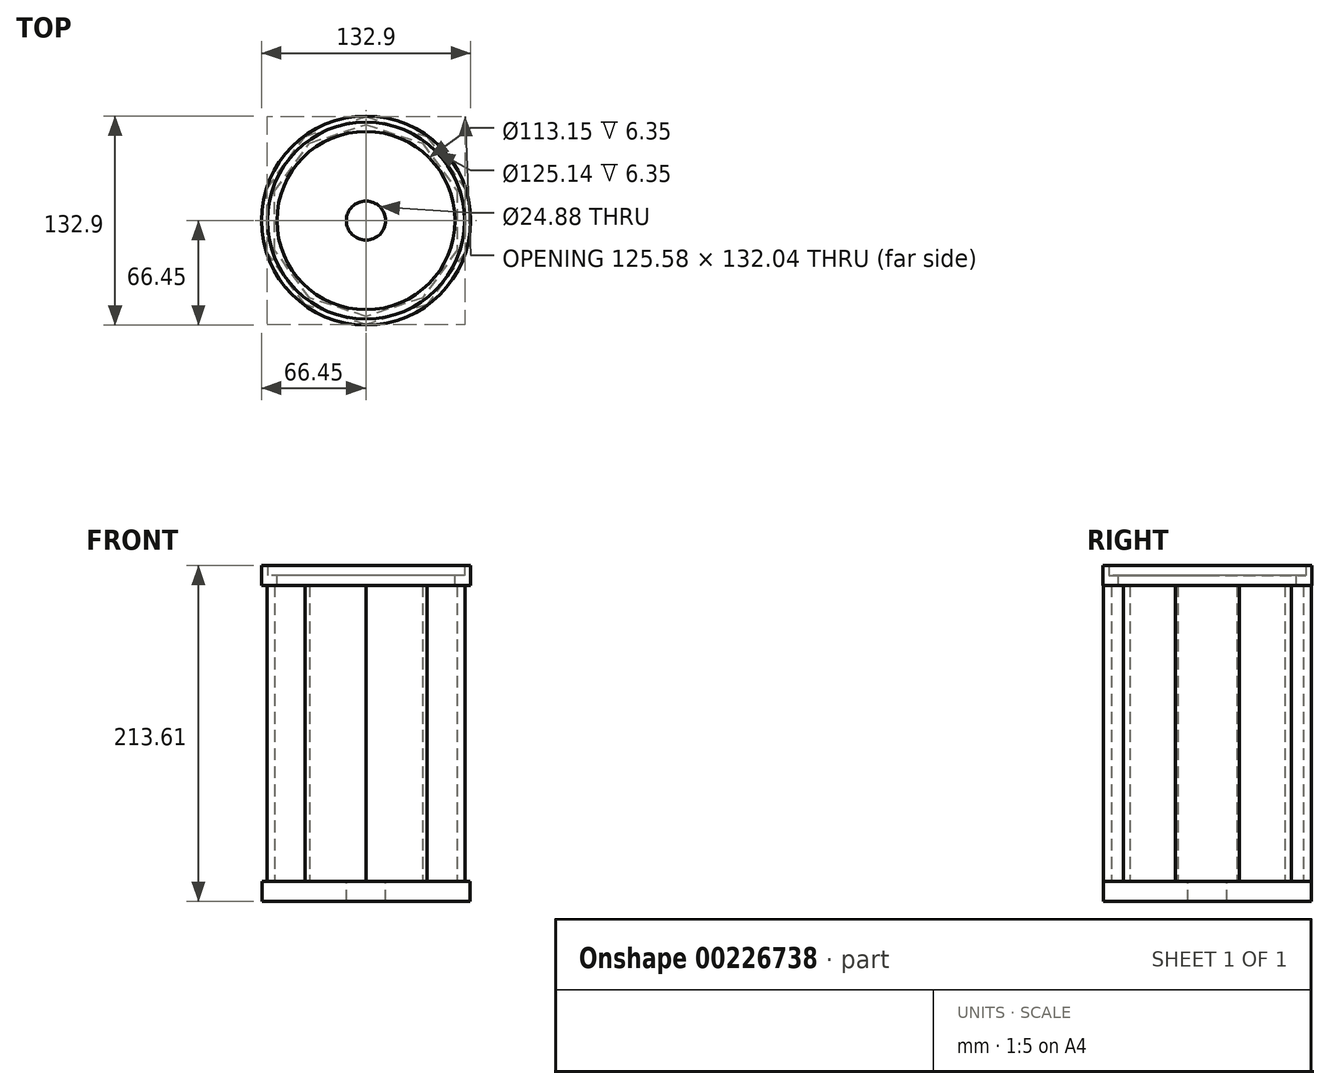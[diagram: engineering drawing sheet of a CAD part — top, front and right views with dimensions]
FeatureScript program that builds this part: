
annotation { "Feature Type Name" : "Feature", "Feature Type Description" : "" }
export const myFeature = defineFeature(function(context is Context, id is Id, definition is map)
    precondition{}
    {
        {
            var Q0;
            Q0=qCreatedBy(makeId("Top.planeOp"),FACE);
            var sketch = newSketch(context, id + "F0", { "sketchPlane" : qUnion([Q0])});
            skCircle(sketch, "E0.cCircle", {"center": v(0, 0) * mm, "radius": 62.79 * mm, "construction": true});
            skLineSegment(sketch, "E0.0", {"start": v(62.79, 20.4) * mm, "end": v(62.79, -20.4) * mm});
            skLineSegment(sketch, "E0.1", {"start": v(62.79, -20.4) * mm, "end": v(38.8, -53.41) * mm});
            skLineSegment(sketch, "E0.2", {"start": v(38.8, -53.41) * mm, "end": v(0, -66.02) * mm});
            skLineSegment(sketch, "E0.3", {"start": v(0, -66.02) * mm, "end": v(-38.8, -53.41) * mm});
            skLineSegment(sketch, "E0.4", {"start": v(-38.8, -53.41) * mm, "end": v(-62.79, -20.4) * mm});
            skLineSegment(sketch, "E0.5", {"start": v(-62.79, -20.4) * mm, "end": v(-62.79, 20.4) * mm});
            skLineSegment(sketch, "E0.6", {"start": v(-62.79, 20.4) * mm, "end": v(-38.8, 53.41) * mm});
            skLineSegment(sketch, "E0.7", {"start": v(-38.8, 53.41) * mm, "end": v(0, 66.02) * mm});
            skLineSegment(sketch, "E0.8", {"start": v(0, 66.02) * mm, "end": v(38.8, 53.41) * mm});
            skLineSegment(sketch, "E0.9", {"start": v(38.8, 53.41) * mm, "end": v(62.79, 20.4) * mm});
            skPoint(sketch, "E0.0.midPoint", {"position": v(62.79, 0) * mm});
            skCircle(sketch, "E1.cCircle", {"center": v(0, 0) * mm, "radius": 57.91 * mm, "construction": true});
            skLineSegment(sketch, "E1.0", {"start": v(57.91, 18.82) * mm, "end": v(57.91, -18.82) * mm});
            skLineSegment(sketch, "E1.1", {"start": v(57.91, -18.82) * mm, "end": v(35.8, -49.26) * mm});
            skLineSegment(sketch, "E1.2", {"start": v(35.8, -49.26) * mm, "end": v(0, -60.9) * mm});
            skLineSegment(sketch, "E1.3", {"start": v(0, -60.9) * mm, "end": v(-35.8, -49.26) * mm});
            skLineSegment(sketch, "E1.4", {"start": v(-35.8, -49.26) * mm, "end": v(-57.91, -18.82) * mm});
            skLineSegment(sketch, "E1.5", {"start": v(-57.91, -18.82) * mm, "end": v(-57.91, 18.82) * mm});
            skLineSegment(sketch, "E1.6", {"start": v(-57.91, 18.82) * mm, "end": v(-35.8, 49.26) * mm});
            skLineSegment(sketch, "E1.7", {"start": v(-35.8, 49.26) * mm, "end": v(0, 60.9) * mm});
            skLineSegment(sketch, "E1.8", {"start": v(0, 60.9) * mm, "end": v(35.8, 49.26) * mm});
            skLineSegment(sketch, "E1.9", {"start": v(35.8, 49.26) * mm, "end": v(57.91, 18.82) * mm});
            skPoint(sketch, "E1.0.midPoint", {"position": v(57.91, 0) * mm});
            skSolve(sketch);
        }
        {
            var Q0;
            Q0=makeQuery(id+"F0.imprint","IMPRINT",FACE,{"disambiguationData":[TD([[makeQuery(id+"F0.imprint","IMPRINT",EDGE,{"derivedFrom":sQuery(id+"F0.wireOp",EDGE,"E0.0")}),-1.0]])]});
            var Q1;
            Q1 = qConstructionFilter(qBodyType(qCreatedBy(id + "F0" ,EDGE), BodyType.WIRE), ConstructionObject.NO);
            extrude(context, id + "F1", {"entities" : qUnion([Q0]), "surfaceEntities" : qUnion([Q1]), "depth" : 188.21 * mm});
        }
        {
            var Q0;
            Q0=qCreatedBy(makeId("Top.planeOp"),FACE);
            var sketch = newSketch(context, id + "F2", { "sketchPlane" : qUnion([Q0])});
            skCircle(sketch, "E2", {"center": v(0, 0) * mm, "radius": 66.14 * mm});
            skSolve(sketch);
        }
        {
            var Q0;
            Q0 = qSketchRegion(id + "F2", true);
            extrude(context, id + "F3", {"entities" : qUnion([Q0]), "operationType" : NewBodyOperationType.ADD, "oppositeDirection" : true, "depth" : 12.7 * mm});
        }
        {
            var Q0;
            Q0=makeQuery(id+"F1.opExtrude","SWEPT_BODY",BODY,{"disambiguationData":[OSD([sQuery(id+"F0.wireOp",EDGE,"E0.0"),sQuery(id+"F0.wireOp",EDGE,"E0.1"),sQuery(id+"F0.wireOp",EDGE,"E0.2"),sQuery(id+"F0.wireOp",EDGE,"E0.3"),sQuery(id+"F0.wireOp",EDGE,"E0.4"),sQuery(id+"F0.wireOp",EDGE,"E0.5"),sQuery(id+"F0.wireOp",EDGE,"E0.6"),sQuery(id+"F0.wireOp",EDGE,"E0.7"),sQuery(id+"F0.wireOp",EDGE,"E0.8"),sQuery(id+"F0.wireOp",EDGE,"E0.9"),sQuery(id+"F0.wireOp",EDGE,"E1.0"),sQuery(id+"F0.wireOp",EDGE,"E1.1"),sQuery(id+"F0.wireOp",EDGE,"E1.2"),sQuery(id+"F0.wireOp",EDGE,"E1.3"),sQuery(id+"F0.wireOp",EDGE,"E1.4"),sQuery(id+"F0.wireOp",EDGE,"E1.5"),sQuery(id+"F0.wireOp",EDGE,"E1.6"),sQuery(id+"F0.wireOp",EDGE,"E1.7"),sQuery(id+"F0.wireOp",EDGE,"E1.8"),sQuery(id+"F0.wireOp",EDGE,"E1.9")])]});
            var Q1;
            Q1=qCreatedBy(makeId("Top.planeOp"),FACE);
            transform(context, id + "F4", {"entities" : qUnion([Q0]), "transformType" : TransformType.TRANSLATION_DISTANCE, "transformDirection" : qUnion([Q1]), "distance" : 188.21 * mm, "oppositeDirection" : true, "makeCopy" : false});
        }
        {
            var Q0;
            Q0=qCreatedBy(makeId("Top.planeOp"),FACE);
            var sketch = newSketch(context, id + "F5", { "sketchPlane" : qUnion([Q0])});
            skCircle(sketch, "E3", {"center": v(0, 0) * mm, "radius": 66.45 * mm});
            skSolve(sketch);
        }
        {
            var Q0;
            Q0 = qSketchRegion(id + "F5", true);
            extrude(context, id + "F6", {"entities" : qUnion([Q0]), "operationType" : NewBodyOperationType.ADD, "depth" : 12.7 * mm});
        }
        {
            var Q0;
            Q0=makeQuery(id+"F1.opExtrude","SWEPT_BODY",BODY,{"disambiguationData":[OSD([sQuery(id+"F0.wireOp",EDGE,"E0.0"),sQuery(id+"F0.wireOp",EDGE,"E0.1"),sQuery(id+"F0.wireOp",EDGE,"E0.2"),sQuery(id+"F0.wireOp",EDGE,"E0.3"),sQuery(id+"F0.wireOp",EDGE,"E0.4"),sQuery(id+"F0.wireOp",EDGE,"E0.5"),sQuery(id+"F0.wireOp",EDGE,"E0.6"),sQuery(id+"F0.wireOp",EDGE,"E0.7"),sQuery(id+"F0.wireOp",EDGE,"E0.8"),sQuery(id+"F0.wireOp",EDGE,"E0.9"),sQuery(id+"F0.wireOp",EDGE,"E1.0"),sQuery(id+"F0.wireOp",EDGE,"E1.1"),sQuery(id+"F0.wireOp",EDGE,"E1.2"),sQuery(id+"F0.wireOp",EDGE,"E1.3"),sQuery(id+"F0.wireOp",EDGE,"E1.4"),sQuery(id+"F0.wireOp",EDGE,"E1.5"),sQuery(id+"F0.wireOp",EDGE,"E1.6"),sQuery(id+"F0.wireOp",EDGE,"E1.7"),sQuery(id+"F0.wireOp",EDGE,"E1.8"),sQuery(id+"F0.wireOp",EDGE,"E1.9")])]});
            var Q1;
            Q1=qCreatedBy(makeId("Top.planeOp"),FACE);
            transform(context, id + "F7", {"entities" : qUnion([Q0]), "transformType" : TransformType.TRANSLATION_DISTANCE, "transformDirection" : qUnion([Q1]), "distance" : 6.35 * mm, "oppositeDirection" : true, "makeCopy" : false});
        }
        {
            var Q0;
            Q0=qCreatedBy(makeId("Top.planeOp"),FACE);
            var sketch = newSketch(context, id + "F8", { "sketchPlane" : qUnion([Q0])});
            skCircle(sketch, "E4", {"center": v(0, 0) * mm, "radius": 62.57 * mm});
            skSolve(sketch);
        }
        {
            var Q0;
            Q0 = qSketchRegion(id + "F8", true);
            extrude(context, id + "F9", {"entities" : qUnion([Q0]), "operationType" : NewBodyOperationType.REMOVE, "depth" : 25.4 * mm});
        }
        {
            var Q0;
            Q0=qCreatedBy(makeId("Top.planeOp"),FACE);
            var sketch = newSketch(context, id + "F10", { "sketchPlane" : qUnion([Q0])});
            skCircle(sketch, "E5", {"center": v(0, 0) * mm, "radius": 56.58 * mm});
            skSolve(sketch);
        }
        {
            var Q0;
            Q0 = qSketchRegion(id + "F10", true);
            extrude(context, id + "F11", {"entities" : qUnion([Q0]), "operationType" : NewBodyOperationType.REMOVE, "oppositeDirection" : true, "depth" : 25.4 * mm});
        }
        {
            var Q0;
            Q0=makeQuery(id+"F1.opExtrude","SWEPT_BODY",BODY,{"disambiguationData":[OSD([sQuery(id+"F0.wireOp",EDGE,"E0.0"),sQuery(id+"F0.wireOp",EDGE,"E0.1"),sQuery(id+"F0.wireOp",EDGE,"E0.2"),sQuery(id+"F0.wireOp",EDGE,"E0.3"),sQuery(id+"F0.wireOp",EDGE,"E0.4"),sQuery(id+"F0.wireOp",EDGE,"E0.5"),sQuery(id+"F0.wireOp",EDGE,"E0.6"),sQuery(id+"F0.wireOp",EDGE,"E0.7"),sQuery(id+"F0.wireOp",EDGE,"E0.8"),sQuery(id+"F0.wireOp",EDGE,"E0.9"),sQuery(id+"F0.wireOp",EDGE,"E1.0"),sQuery(id+"F0.wireOp",EDGE,"E1.1"),sQuery(id+"F0.wireOp",EDGE,"E1.2"),sQuery(id+"F0.wireOp",EDGE,"E1.3"),sQuery(id+"F0.wireOp",EDGE,"E1.4"),sQuery(id+"F0.wireOp",EDGE,"E1.5"),sQuery(id+"F0.wireOp",EDGE,"E1.6"),sQuery(id+"F0.wireOp",EDGE,"E1.7"),sQuery(id+"F0.wireOp",EDGE,"E1.8"),sQuery(id+"F0.wireOp",EDGE,"E1.9")])]});
            var Q1;
            Q1=qCreatedBy(makeId("Top.planeOp"),FACE);
            transform(context, id + "F12", {"entities" : qUnion([Q0]), "transformType" : TransformType.TRANSLATION_DISTANCE, "transformDirection" : qUnion([Q1]), "distance" : 194.56 * mm, "makeCopy" : false});
        }
        {
            var Q0;
            Q0=qCreatedBy(makeId("Top.planeOp"),FACE);
            var sketch = newSketch(context, id + "F13", { "sketchPlane" : qUnion([Q0])});
            skCircle(sketch, "E6", {"center": v(0, 0) * mm, "radius": 12.44 * mm});
            skSolve(sketch);
        }
        {
            var Q0;
            Q0 = qSketchRegion(id + "F13", true);
            extrude(context, id + "F14", {"entities" : qUnion([Q0]), "operationType" : NewBodyOperationType.REMOVE, "oppositeDirection" : true, "depth" : 25.4 * mm});
        }
        {
            var Q0;
            Q0=makeQuery(id+"F1.opExtrude","SWEPT_BODY",BODY,{"disambiguationData":[OSD([sQuery(id+"F0.wireOp",EDGE,"E0.0"),sQuery(id+"F0.wireOp",EDGE,"E0.1"),sQuery(id+"F0.wireOp",EDGE,"E0.2"),sQuery(id+"F0.wireOp",EDGE,"E0.3"),sQuery(id+"F0.wireOp",EDGE,"E0.4"),sQuery(id+"F0.wireOp",EDGE,"E0.5"),sQuery(id+"F0.wireOp",EDGE,"E0.6"),sQuery(id+"F0.wireOp",EDGE,"E0.7"),sQuery(id+"F0.wireOp",EDGE,"E0.8"),sQuery(id+"F0.wireOp",EDGE,"E0.9"),sQuery(id+"F0.wireOp",EDGE,"E1.0"),sQuery(id+"F0.wireOp",EDGE,"E1.1"),sQuery(id+"F0.wireOp",EDGE,"E1.2"),sQuery(id+"F0.wireOp",EDGE,"E1.3"),sQuery(id+"F0.wireOp",EDGE,"E1.4"),sQuery(id+"F0.wireOp",EDGE,"E1.5"),sQuery(id+"F0.wireOp",EDGE,"E1.6"),sQuery(id+"F0.wireOp",EDGE,"E1.7"),sQuery(id+"F0.wireOp",EDGE,"E1.8"),sQuery(id+"F0.wireOp",EDGE,"E1.9")])]});
            var Q1;
            Q1=qCreatedBy(makeId("Top.planeOp"),FACE);
            transform(context, id + "F15", {"entities" : qUnion([Q0]), "transformType" : TransformType.TRANSLATION_DISTANCE, "transformDirection" : qUnion([Q1]), "distance" : 194.56 * mm, "oppositeDirection" : true, "makeCopy" : false});
        }
    });
